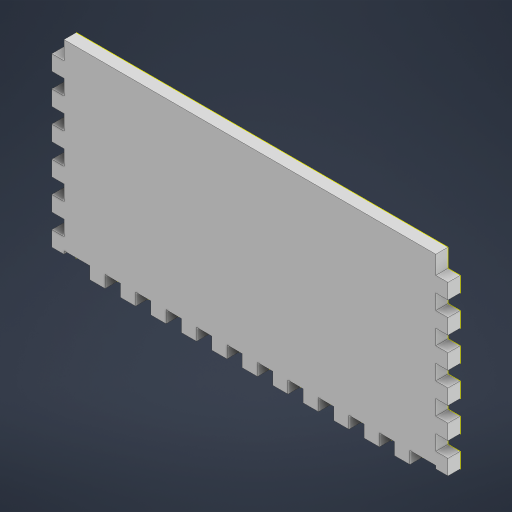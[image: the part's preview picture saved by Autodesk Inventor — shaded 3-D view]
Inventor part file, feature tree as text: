
AUTODESK INVENTOR PART (.ipt)
format: ipt  version: 2023 (Build 270158030, 158C)  size: 301,056 bytes
history: native  units: mm
features: sketch x2, extrude x1, projected_geometry x1
ambient origin geometry x8: Origin, YZ Plane, XZ Plane, XY Plane, X Axis, Y Axis, Z Axis, Center Point
bodies: Solid1 (feature_tree)
feature tree (4):
  extrude  "Extrusion1"  [1 undecoded]
  sketch  "Sketch2"
  sketch  "Sketch1"  dims[d0=4.0mm d1=0.0mm]
  projected_geometry  "Projected Loop1"
note: 1 required parameter value undecoded (feature->parameter linkage not recoverable at this tier; creation-order binding heuristic only, values carry confidence <= 0.55)
